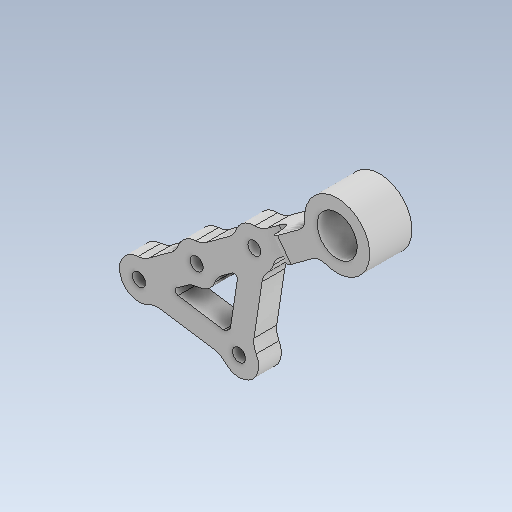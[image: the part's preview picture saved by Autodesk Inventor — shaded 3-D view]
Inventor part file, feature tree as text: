
AUTODESK INVENTOR PART (.ipt)
format: ipt  version: 2020 (Build 240168000, 168)  size: 244,736 bytes
history: native  units: mm
features: sketch x8, other x3, plane x1
ambient origin geometry x8: Origin, YZ Plane, XZ Plane, XY Plane, X Axis, Y Axis, Z Axis, Center Point
bodies: Solid1 (feature_tree)
feature tree (12):
  other  "leg_link_4.ipt"
  other  "Solid1::leg_link_4.ipt"
  other  "TaggingFeature1"
  sketch  "Sketch1"  dims[d0=10.0mm]
  sketch  "Sketch2"
  sketch  "Sketch3"
  sketch  "Sketch4"
  sketch  "Sketch5"
  sketch  "Sketch6"
  sketch  "Sketch7"
  sketch  "Sketch8"
  plane  "Work Plane1"
